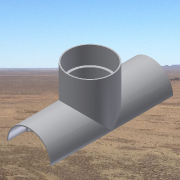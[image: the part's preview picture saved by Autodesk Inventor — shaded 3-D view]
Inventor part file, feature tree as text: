
AUTODESK INVENTOR PART (.ipt)
format: ipt  version: 2013 SP2 (Build 170200200, 200)  size: 207,872 bytes
history: native  units: in
note: dims shown in document units (in); Inventor stores cm internally (conversion verified against a paired STEP export)
features: sketch x9, extrude x8, plane x1
ambient origin geometry x8: Origin, YZ Plane, XZ Plane, XY Plane, X Axis, Y Axis, Z Axis, Center Point
bodies: Solid1 (feature_tree)
feature tree (18):
  extrude  "mainBody"  Depth=6.875in TaperAngle=0.0deg
  sketch  "Sketch10"  dims[d29=3.4375in d30=2.5in]
  plane  "Work Plane5"
  extrude  "TBody"  Depth=2.5in
  extrude  "TSocket"  Depth=2.375in
  extrude  "TTube"  Depth=2.1in
  extrude  "mainTube"  Depth=2.1in
  extrude  "mainSocket1"  Depth=2.375in
  extrude  "mainSocket2"  Depth=2.375in
  extrude  "Extrusion18"  Depth=8.0in TaperAngle=0.0deg
  sketch  "Sketch1"  dims[d0=2.5in d1=6.875in d2=0.0in]
  sketch  "Sketch11"  dims[d31=1.5in d32=1.25in d33=0.0in d34=0.0in d35=2.375in]
  sketch  "Sketch12"  dims[d37=1.0in d38=0.0in d39=2.1in]
  sketch  "Sketch13"  dims[d41=1.5in d42=0.0in d43=2.1in]
  sketch  "Sketch14"  dims[d45=7.0in d46=0.0in d47=2.375in]
  sketch  "Sketch15"  dims[d49=1.0in d50=0.0in d51=2.375in]
  sketch  "Sketch16"  dims[d53=1.0in d54=0.0in d66=8.0in d67=0.0in]
  sketch  "Sketch21"
